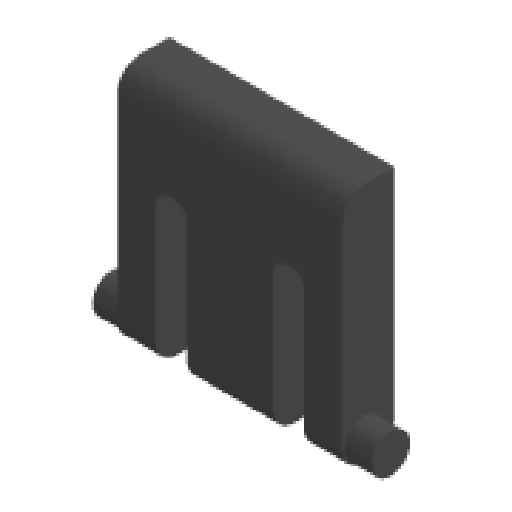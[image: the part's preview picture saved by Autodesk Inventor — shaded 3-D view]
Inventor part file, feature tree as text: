
AUTODESK INVENTOR PART (.ipt)
format: ipt  version: 2025 (Build 290162000, 162)  size: 186,880 bytes
history: native  units: mm
features: extrude x4, sketch x4, fillet x2, mirror x1
ambient origin geometry x8: Origin, YZ Plane, XZ Plane, XY Plane, X Axis, Y Axis, Z Axis, Center Point
bodies: Solid1 (feature_tree)
feature tree (11):
  extrude  "Extrusion1"  Depth=11.7mm
  extrude  "Extrusion3"  Depth=2.6mm
  extrude  "Extrusion4"  Depth=1.4mm TaperAngle=0.0deg
  mirror  "Mirror1"
  extrude  "Extrusion5"  Depth=1.6mm
  fillet  "Fillet1"  Radius=8.0mm
  fillet  "Fillet3"  [1 undecoded]
  sketch  "Sketch1"  dims[d0=12.5mm d1=11.7mm]
  sketch  "Sketch3"  dims[d2=2.6mm d3=0.0mm d10=2.1mm]
  sketch  "Sketch4"  dims[d11=0.1mm d13=1.4mm d14=0.0mm]
  sketch  "Sketch6"  dims[d18=2.0mm d19=1.6mm d20=8.0mm d21=0.0mm d22=0.0mm d23=0.1mm d32=3.0mm d34=3.0mm d35=0.0mm d36=0.0mm d37=0.6mm d40=1.2mm d49=0.2mm d50=2.0mm d51=5.0mm]
note: 1 required parameter value undecoded (feature->parameter linkage not recoverable at this tier; creation-order binding heuristic only, values carry confidence <= 0.55)
